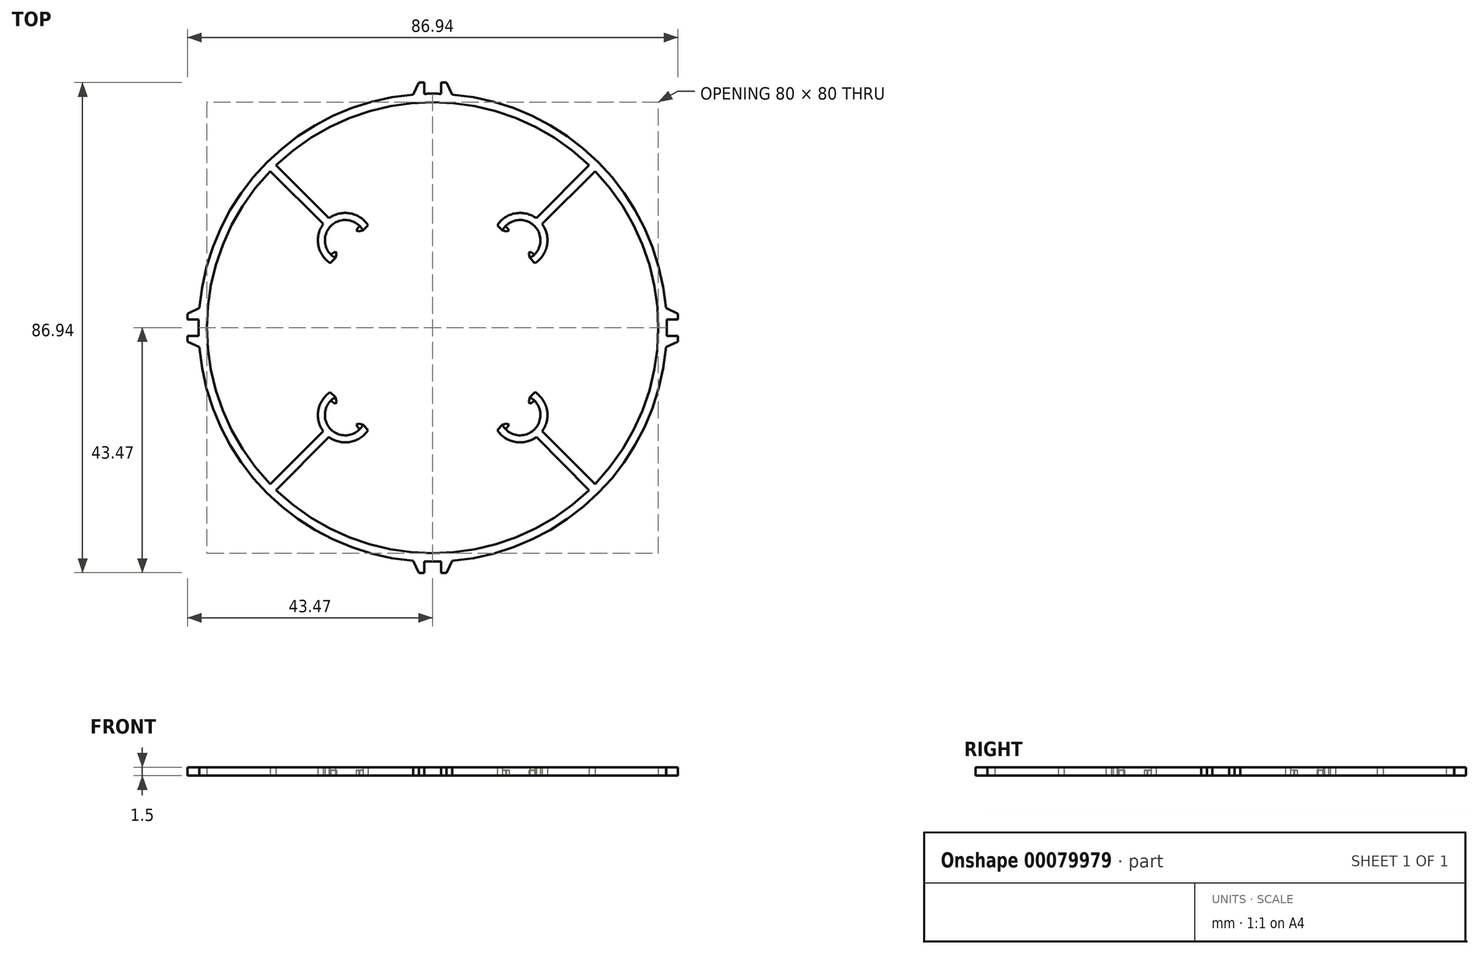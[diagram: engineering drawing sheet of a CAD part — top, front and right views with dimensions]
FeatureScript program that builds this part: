
annotation { "Feature Type Name" : "Feature", "Feature Type Description" : "" }
export const myFeature = defineFeature(function(context is Context, id is Id, definition is map)
    precondition{}
    {
        {
            var Q0;
            Q0=qCreatedBy(makeId("Top.planeOp"),FACE);
            var sketch = newSketch(context, id + "F0", { "sketchPlane" : qUnion([Q0])});
            skLineSegment(sketch, "E0.bottom", {"start": v(-15.5, 15.5) * mm, "end": v(15.5, 15.5) * mm});
            skLineSegment(sketch, "E0.top", {"start": v(-15.5, -15.5) * mm, "end": v(15.5, -15.5) * mm});
            skLineSegment(sketch, "E0.left", {"start": v(-15.5, 15.5) * mm, "end": v(-15.5, -15.5) * mm});
            skLineSegment(sketch, "E0.right", {"start": v(15.5, 15.5) * mm, "end": v(15.5, -15.5) * mm});
            skPoint(sketch, "E0.middle", {"position": v(0, 0) * mm});
            skCircle(sketch, "E1", {"center": v(-15.5, 15.5) * mm, "radius": 15 * mm});
            skCircle(sketch, "E2", {"center": v(15.5, 15.5) * mm, "radius": 15 * mm});
            skCircle(sketch, "E3", {"center": v(-15.5, -15.5) * mm, "radius": 15 * mm});
            skCircle(sketch, "E4", {"center": v(15.5, -15.5) * mm, "radius": 15 * mm});
            skLineSegment(sketch, "E5.bottom", {"start": v(-10, 10) * mm, "end": v(10, 10) * mm});
            skLineSegment(sketch, "E5.top", {"start": v(-10, -10) * mm, "end": v(10, -10) * mm});
            skLineSegment(sketch, "E5.left", {"start": v(-10, 10) * mm, "end": v(-10, -10) * mm});
            skLineSegment(sketch, "E5.right", {"start": v(10, 10) * mm, "end": v(10, -10) * mm});
            skCircle(sketch, "E6", {"center": v(-15.5, 15.5) * mm, "radius": 4.5 * mm});
            skCircle(sketch, "E7", {"center": v(-15.5, 15.5) * mm, "radius": 3.5 * mm});
            skCircle(sketch, "E8", {"center": v(15.5, 15.5) * mm, "radius": 3.5 * mm});
            skCircle(sketch, "E9", {"center": v(15.5, 15.5) * mm, "radius": 4.5 * mm});
            skCircle(sketch, "E10", {"center": v(15.5, -15.5) * mm, "radius": 4.5 * mm});
            skCircle(sketch, "E11", {"center": v(15.5, -15.5) * mm, "radius": 3.5 * mm});
            skCircle(sketch, "E12", {"center": v(-15.5, -15.5) * mm, "radius": 3.5 * mm});
            skCircle(sketch, "E13", {"center": v(-15.5, -15.5) * mm, "radius": 4.5 * mm});
            skLineSegment(sketch, "E14.bottom", {"start": v(-15.5, 15.5) * mm, "end": v(-10.5, 15.5) * mm});
            skLineSegment(sketch, "E14.left", {"start": v(-15.5, 15.5) * mm, "end": v(-15.5, 20.5) * mm});
            skLineSegment(sketch, "E15", {"start": v(-12.32, 18.68) * mm, "end": v(-18.68, 12.32) * mm});
            skLineSegment(sketch, "E16", {"start": v(-17.9, 11.7) * mm, "end": v(-11.7, 17.9) * mm});
            skSolve(sketch);
        }
        {
            var Q0;
            {var subQ1=sQuery(id+"F0.wireOp",EDGE,"E0.bottom");var subQ5=sQuery(id+"F0.wireOp",EDGE,"E14.bottom");var subQ6=makeQuery(id+"F0.imprint","INTERSECT",VERTEX,{"derivedFrom":[subQ1,subQ5]});Q0=makeQuery(id+"F0.imprint","IMPRINT",FACE,{"disambiguationData":[TD([[makeQuery(id+"F0.imprint","IMPRINT",EDGE,{"disambiguationData":[TD([[subQ6,-1.0]])],"derivedFrom":subQ1}),1.0]])]});}
            var sketch = newSketch(context, id + "F1", { "sketchPlane" : qUnion([Q0])});
            skCircle(sketch, "E17", {"center": v(0, 0) * mm, "radius": 41.5 * mm});
            skLineSegment(sketch, "E18", {"start": v(-17.05, 13.08) * mm, "end": v(-17.24, 13.54) * mm});
            skLineSegment(sketch, "E19", {"start": v(-17.24, 13.54) * mm, "end": v(-18.05, 12.95) * mm});
            skLineSegment(sketch, "E20", {"start": v(-18.39, 19.4) * mm, "end": v(-27.75, 28.8) * mm});
            skLineSegment(sketch, "E21", {"start": v(-19.4, 18.39) * mm, "end": v(-28.8, 27.75) * mm});
            skLineSegment(sketch, "E22", {"start": v(-17.25, 12.35) * mm, "end": v(-17.05, 13.08) * mm});
            skArc(sketch, "E23", {"start": v(-11.44, 18.16) * mm, "mid": v(-14.65, 20.27) * mm, "end": v(-18.39, 19.4) * mm});
            skArc(sketch, "E24", {"start": v(-12.95, 18.05) * mm, "mid": v(-18.05, 18.05) * mm, "end": v(-18.05, 12.95) * mm});
            skLineSegment(sketch, "E25.0", {"start": v(-17.9, 11.7) * mm, "end": v(-11.7, 17.9) * mm, "construction": true});
            skLineSegment(sketch, "E26", {"start": v(-12.95, 18.05) * mm, "end": v(-13.54, 17.24) * mm});
            skLineSegment(sketch, "E27", {"start": v(-13.54, 17.24) * mm, "end": v(-13.08, 17.05) * mm});
            skLineSegment(sketch, "E28", {"start": v(-13.08, 17.05) * mm, "end": v(-12.35, 17.25) * mm});
            skLineSegment(sketch, "E29", {"start": v(-12.35, 17.25) * mm, "end": v(-11.7, 17.9) * mm, "construction": true});
            skArc(sketch, "E30", {"start": v(-28.8, 27.75) * mm, "mid": v(-40, 0) * mm, "end": v(-28.8, -27.75) * mm});
            skLineSegment(sketch, "E31", {"start": v(-12.35, 17.25) * mm, "end": v(-11.44, 18.16) * mm});
            skLineSegment(sketch, "E32", {"start": v(-18.16, 11.44) * mm, "end": v(-17.25, 12.35) * mm});
            skArc(sketch, "E33.trimOffspring", {"start": v(-19.4, 18.39) * mm, "mid": v(-20.27, 14.65) * mm, "end": v(-18.16, 11.44) * mm});
            skArc(sketch, "E34.1.0", {"start": v(-18.39, -19.4) * mm, "mid": v(-14.65, -20.27) * mm, "end": v(-11.44, -18.16) * mm});
            skLineSegment(sketch, "E34.1.1", {"start": v(-19.4, -18.39) * mm, "end": v(-28.8, -27.75) * mm});
            skArc(sketch, "E34.1.2", {"start": v(-18.05, -12.95) * mm, "mid": v(-18.05, -18.05) * mm, "end": v(-12.95, -18.05) * mm});
            skLineSegment(sketch, "E34.1.3", {"start": v(-11.7, -17.9) * mm, "end": v(-17.9, -11.7) * mm, "construction": true});
            skArc(sketch, "E34.1.4", {"start": v(-18.16, -11.44) * mm, "mid": v(-20.27, -14.65) * mm, "end": v(-19.4, -18.39) * mm});
            skLineSegment(sketch, "E34.1.5", {"start": v(-18.39, -19.4) * mm, "end": v(-27.75, -28.8) * mm});
            skLineSegment(sketch, "E34.1.6", {"start": v(-18.05, -12.95) * mm, "end": v(-17.24, -13.54) * mm});
            skLineSegment(sketch, "E34.1.7", {"start": v(-13.54, -17.24) * mm, "end": v(-12.95, -18.05) * mm});
            skLineSegment(sketch, "E34.1.8", {"start": v(-17.05, -13.08) * mm, "end": v(-17.25, -12.35) * mm});
            skLineSegment(sketch, "E34.1.9", {"start": v(-17.24, -13.54) * mm, "end": v(-17.05, -13.08) * mm});
            skLineSegment(sketch, "E34.1.10", {"start": v(-11.44, -18.16) * mm, "end": v(-12.35, -17.25) * mm});
            skLineSegment(sketch, "E34.1.11", {"start": v(-12.35, -17.25) * mm, "end": v(-13.08, -17.05) * mm});
            skLineSegment(sketch, "E34.1.12", {"start": v(-17.25, -12.35) * mm, "end": v(-18.16, -11.44) * mm});
            skLineSegment(sketch, "E34.1.13", {"start": v(-13.08, -17.05) * mm, "end": v(-13.54, -17.24) * mm});
            skLineSegment(sketch, "E34.1.14", {"start": v(-17.25, -12.35) * mm, "end": v(-17.9, -11.7) * mm, "construction": true});
            skArc(sketch, "E34.2.0", {"start": v(19.4, -18.39) * mm, "mid": v(20.27, -14.65) * mm, "end": v(18.16, -11.44) * mm});
            skLineSegment(sketch, "E34.2.1", {"start": v(18.39, -19.4) * mm, "end": v(27.75, -28.8) * mm});
            skArc(sketch, "E34.2.2", {"start": v(12.95, -18.05) * mm, "mid": v(18.05, -18.05) * mm, "end": v(18.05, -12.95) * mm});
            skLineSegment(sketch, "E34.2.3", {"start": v(17.9, -11.7) * mm, "end": v(11.7, -17.9) * mm, "construction": true});
            skArc(sketch, "E34.2.4", {"start": v(11.44, -18.16) * mm, "mid": v(14.65, -20.27) * mm, "end": v(18.39, -19.4) * mm});
            skLineSegment(sketch, "E34.2.5", {"start": v(19.4, -18.39) * mm, "end": v(28.8, -27.75) * mm});
            skLineSegment(sketch, "E34.2.6", {"start": v(12.95, -18.05) * mm, "end": v(13.54, -17.24) * mm});
            skLineSegment(sketch, "E34.2.7", {"start": v(17.24, -13.54) * mm, "end": v(18.05, -12.95) * mm});
            skLineSegment(sketch, "E34.2.8", {"start": v(13.08, -17.05) * mm, "end": v(12.35, -17.25) * mm});
            skLineSegment(sketch, "E34.2.9", {"start": v(13.54, -17.24) * mm, "end": v(13.08, -17.05) * mm});
            skLineSegment(sketch, "E34.2.10", {"start": v(18.16, -11.44) * mm, "end": v(17.25, -12.35) * mm});
            skLineSegment(sketch, "E34.2.11", {"start": v(17.25, -12.35) * mm, "end": v(17.05, -13.08) * mm});
            skLineSegment(sketch, "E34.2.12", {"start": v(12.35, -17.25) * mm, "end": v(11.44, -18.16) * mm});
            skLineSegment(sketch, "E34.2.13", {"start": v(17.05, -13.08) * mm, "end": v(17.24, -13.54) * mm});
            skLineSegment(sketch, "E34.2.14", {"start": v(12.35, -17.25) * mm, "end": v(11.7, -17.9) * mm, "construction": true});
            skArc(sketch, "E34.3.0", {"start": v(18.39, 19.4) * mm, "mid": v(14.65, 20.27) * mm, "end": v(11.44, 18.16) * mm});
            skLineSegment(sketch, "E34.3.1", {"start": v(19.4, 18.39) * mm, "end": v(28.8, 27.75) * mm});
            skArc(sketch, "E34.3.2", {"start": v(18.05, 12.95) * mm, "mid": v(18.05, 18.05) * mm, "end": v(12.95, 18.05) * mm});
            skLineSegment(sketch, "E34.3.3", {"start": v(11.7, 17.9) * mm, "end": v(17.9, 11.7) * mm, "construction": true});
            skArc(sketch, "E34.3.4", {"start": v(18.16, 11.44) * mm, "mid": v(20.27, 14.65) * mm, "end": v(19.4, 18.39) * mm});
            skLineSegment(sketch, "E34.3.5", {"start": v(18.39, 19.4) * mm, "end": v(27.75, 28.8) * mm});
            skLineSegment(sketch, "E34.3.6", {"start": v(18.05, 12.95) * mm, "end": v(17.24, 13.54) * mm});
            skLineSegment(sketch, "E34.3.7", {"start": v(13.54, 17.24) * mm, "end": v(12.95, 18.05) * mm});
            skLineSegment(sketch, "E34.3.8", {"start": v(17.05, 13.08) * mm, "end": v(17.25, 12.35) * mm});
            skLineSegment(sketch, "E34.3.9", {"start": v(17.24, 13.54) * mm, "end": v(17.05, 13.08) * mm});
            skLineSegment(sketch, "E34.3.10", {"start": v(11.44, 18.16) * mm, "end": v(12.35, 17.25) * mm});
            skLineSegment(sketch, "E34.3.11", {"start": v(12.35, 17.25) * mm, "end": v(13.08, 17.05) * mm});
            skLineSegment(sketch, "E34.3.12", {"start": v(17.25, 12.35) * mm, "end": v(18.16, 11.44) * mm});
            skLineSegment(sketch, "E34.3.13", {"start": v(13.08, 17.05) * mm, "end": v(13.54, 17.24) * mm});
            skLineSegment(sketch, "E34.3.14", {"start": v(17.25, 12.35) * mm, "end": v(17.9, 11.7) * mm, "construction": true});
            skArc(sketch, "E35.trimOffspring", {"start": v(27.75, 28.8) * mm, "mid": v(0, 40) * mm, "end": v(-27.75, 28.8) * mm});
            skArc(sketch, "E36.trimOffspring", {"start": v(28.8, -27.75) * mm, "mid": v(40, 0) * mm, "end": v(28.8, 27.75) * mm});
            skArc(sketch, "E37.trimOffspring", {"start": v(-27.75, -28.8) * mm, "mid": v(0, -40) * mm, "end": v(27.75, -28.8) * mm});
            skSolve(sketch);
        }
        {
            var Q0;
            Q0=qCreatedBy(makeId("Top.planeOp"),FACE);
            var sketch = newSketch(context, id + "F2", { "sketchPlane" : qUnion([Q0])});
            skLineSegment(sketch, "E38", {"start": v(-1.47, 43.47) * mm, "end": v(-2.47, 43.47) * mm});
            skLineSegment(sketch, "E39", {"start": v(-2.47, 43.47) * mm, "end": v(-3.46, 41.36) * mm});
            skLineSegment(sketch, "E40.MirrorCS", {"start": v(1.47, 43.47) * mm, "end": v(2.47, 43.47) * mm});
            skLineSegment(sketch, "E41.MirrorCS", {"start": v(2.47, 43.47) * mm, "end": v(3.46, 41.36) * mm});
            skLineSegment(sketch, "E42", {"start": v(-1.47, 43.47) * mm, "end": v(-1.47, 41.47) * mm});
            skLineSegment(sketch, "E43", {"start": v(1.47, 43.47) * mm, "end": v(1.47, 41.47) * mm});
            skLineSegment(sketch, "E44.1.0", {"start": v(-43.47, 1.47) * mm, "end": v(-43.47, 2.47) * mm});
            skLineSegment(sketch, "E44.1.1", {"start": v(-43.47, -1.47) * mm, "end": v(-43.47, -2.47) * mm});
            skLineSegment(sketch, "E44.1.2", {"start": v(-43.47, 2.47) * mm, "end": v(-41.36, 3.46) * mm});
            skLineSegment(sketch, "E44.1.3", {"start": v(-43.47, -2.47) * mm, "end": v(-41.36, -3.46) * mm});
            skLineSegment(sketch, "E44.1.4", {"start": v(-43.47, 1.47) * mm, "end": v(-41.47, 1.47) * mm});
            skLineSegment(sketch, "E44.1.5", {"start": v(-43.47, -1.47) * mm, "end": v(-41.47, -1.47) * mm});
            skLineSegment(sketch, "E44.2.0", {"start": v(-1.47, -43.47) * mm, "end": v(-2.47, -43.47) * mm});
            skLineSegment(sketch, "E44.2.1", {"start": v(1.47, -43.47) * mm, "end": v(2.47, -43.47) * mm});
            skLineSegment(sketch, "E44.2.2", {"start": v(-2.47, -43.47) * mm, "end": v(-3.46, -41.36) * mm});
            skLineSegment(sketch, "E44.2.3", {"start": v(2.47, -43.47) * mm, "end": v(3.46, -41.36) * mm});
            skLineSegment(sketch, "E44.2.4", {"start": v(-1.47, -43.47) * mm, "end": v(-1.47, -41.47) * mm});
            skLineSegment(sketch, "E44.2.5", {"start": v(1.47, -43.47) * mm, "end": v(1.47, -41.47) * mm});
            skLineSegment(sketch, "E44.3.0", {"start": v(43.47, -1.47) * mm, "end": v(43.47, -2.47) * mm});
            skLineSegment(sketch, "E44.3.1", {"start": v(43.47, 1.47) * mm, "end": v(43.47, 2.47) * mm});
            skLineSegment(sketch, "E44.3.2", {"start": v(43.47, -2.47) * mm, "end": v(41.36, -3.46) * mm});
            skLineSegment(sketch, "E44.3.3", {"start": v(43.47, 2.47) * mm, "end": v(41.36, 3.46) * mm});
            skLineSegment(sketch, "E44.3.4", {"start": v(43.47, -1.47) * mm, "end": v(41.47, -1.47) * mm});
            skLineSegment(sketch, "E44.3.5", {"start": v(43.47, 1.47) * mm, "end": v(41.47, 1.47) * mm});
            skPoint(sketch, "E44.center", {"position": v(0, 0) * mm});
            skLineSegment(sketch, "E45", {"start": v(-41.47, 1.47) * mm, "end": v(-41.36, 3.46) * mm});
            skLineSegment(sketch, "E46", {"start": v(-41.36, -3.46) * mm, "end": v(-41.47, -1.47) * mm});
            skLineSegment(sketch, "E47", {"start": v(-3.46, 41.36) * mm, "end": v(-1.47, 41.47) * mm});
            skLineSegment(sketch, "E48", {"start": v(1.47, 41.47) * mm, "end": v(3.46, 41.36) * mm});
            skLineSegment(sketch, "E49", {"start": v(41.36, 3.46) * mm, "end": v(41.47, 1.47) * mm});
            skLineSegment(sketch, "E50", {"start": v(41.47, -1.47) * mm, "end": v(41.36, -3.46) * mm});
            skLineSegment(sketch, "E51", {"start": v(1.47, -41.47) * mm, "end": v(3.46, -41.36) * mm});
            skLineSegment(sketch, "E52", {"start": v(-1.47, -41.47) * mm, "end": v(-3.46, -41.36) * mm});
            skSolve(sketch);
        }
        {
            var Q0;
            Q0=qSketchRegion(id+"F1",true);
            extrude(context, id + "F3", {"entities" : qUnion([Q0]), "depth" : 1.5 * mm});
        }
        {
            var Q0;
            Q0=qSketchRegion(id+"F2",true);
            extrude(context, id + "F4", {"entities" : qUnion([Q0]), "operationType" : NewBodyOperationType.ADD, "depth" : 1.5 * mm});
        }
        {
            var Q0;
            Q0=makeQuery(id+"F4.boolean.opBoolean","MERGE",FACE,{"derivedFrom":[makeQuery(id+"F3.opExtrude","CAP_FACE",FACE,{"disambiguationData":[OSD([sQuery(id+"F1.wireOp",EDGE,"E17"),sQuery(id+"F1.wireOp",EDGE,"E18"),sQuery(id+"F1.wireOp",EDGE,"E19"),sQuery(id+"F1.wireOp",EDGE,"E20"),sQuery(id+"F1.wireOp",EDGE,"E21"),sQuery(id+"F1.wireOp",EDGE,"E22"),sQuery(id+"F1.wireOp",EDGE,"E23"),sQuery(id+"F1.wireOp",EDGE,"E24"),sQuery(id+"F1.wireOp",EDGE,"E26"),sQuery(id+"F1.wireOp",EDGE,"E27"),sQuery(id+"F1.wireOp",EDGE,"E28"),sQuery(id+"F1.wireOp",EDGE,"E30"),sQuery(id+"F1.wireOp",EDGE,"E31"),sQuery(id+"F1.wireOp",EDGE,"E32"),sQuery(id+"F1.wireOp",EDGE,"E33.trimOffspring"),sQuery(id+"F1.wireOp",EDGE,"E34.1.0"),sQuery(id+"F1.wireOp",EDGE,"E34.1.1"),sQuery(id+"F1.wireOp",EDGE,"E34.1.2"),sQuery(id+"F1.wireOp",EDGE,"E34.1.4"),sQuery(id+"F1.wireOp",EDGE,"E34.1.5"),sQuery(id+"F1.wireOp",EDGE,"E34.1.6"),sQuery(id+"F1.wireOp",EDGE,"E34.1.7"),sQuery(id+"F1.wireOp",EDGE,"E34.1.8"),sQuery(id+"F1.wireOp",EDGE,"E34.1.9"),sQuery(id+"F1.wireOp",EDGE,"E34.1.10"),sQuery(id+"F1.wireOp",EDGE,"E34.1.11"),sQuery(id+"F1.wireOp",EDGE,"E34.1.12"),sQuery(id+"F1.wireOp",EDGE,"E34.1.13"),sQuery(id+"F1.wireOp",EDGE,"E34.2.0"),sQuery(id+"F1.wireOp",EDGE,"E34.2.1"),sQuery(id+"F1.wireOp",EDGE,"E34.2.2"),sQuery(id+"F1.wireOp",EDGE,"E34.2.4"),sQuery(id+"F1.wireOp",EDGE,"E34.2.5"),sQuery(id+"F1.wireOp",EDGE,"E34.2.6"),sQuery(id+"F1.wireOp",EDGE,"E34.2.7"),sQuery(id+"F1.wireOp",EDGE,"E34.2.8"),sQuery(id+"F1.wireOp",EDGE,"E34.2.9"),sQuery(id+"F1.wireOp",EDGE,"E34.2.10"),sQuery(id+"F1.wireOp",EDGE,"E34.2.11"),sQuery(id+"F1.wireOp",EDGE,"E34.2.12"),sQuery(id+"F1.wireOp",EDGE,"E34.2.13"),sQuery(id+"F1.wireOp",EDGE,"E34.3.0"),sQuery(id+"F1.wireOp",EDGE,"E34.3.1"),sQuery(id+"F1.wireOp",EDGE,"E34.3.2"),sQuery(id+"F1.wireOp",EDGE,"E34.3.4"),sQuery(id+"F1.wireOp",EDGE,"E34.3.5"),sQuery(id+"F1.wireOp",EDGE,"E34.3.6"),sQuery(id+"F1.wireOp",EDGE,"E34.3.7"),sQuery(id+"F1.wireOp",EDGE,"E34.3.8"),sQuery(id+"F1.wireOp",EDGE,"E34.3.9"),sQuery(id+"F1.wireOp",EDGE,"E34.3.10"),sQuery(id+"F1.wireOp",EDGE,"E34.3.11"),sQuery(id+"F1.wireOp",EDGE,"E34.3.12"),sQuery(id+"F1.wireOp",EDGE,"E34.3.13"),sQuery(id+"F1.wireOp",EDGE,"E35.trimOffspring"),sQuery(id+"F1.wireOp",EDGE,"E36.trimOffspring"),sQuery(id+"F1.wireOp",EDGE,"E37.trimOffspring")])],"isStart":false}),makeQuery(id+"F4.opExtrude","CAP_FACE",FACE,{"disambiguationData":[OSD([sQuery(id+"F2.wireOp",EDGE,"E38"),sQuery(id+"F2.wireOp",EDGE,"E39"),sQuery(id+"F2.wireOp",EDGE,"E42"),sQuery(id+"F2.wireOp",EDGE,"E47")])],"isStart":false}),makeQuery(id+"F4.opExtrude","CAP_FACE",FACE,{"disambiguationData":[OSD([sQuery(id+"F2.wireOp",EDGE,"E40.MirrorCS"),sQuery(id+"F2.wireOp",EDGE,"E41.MirrorCS"),sQuery(id+"F2.wireOp",EDGE,"E43"),sQuery(id+"F2.wireOp",EDGE,"E48")])],"isStart":false}),makeQuery(id+"F4.opExtrude","CAP_FACE",FACE,{"disambiguationData":[OSD([sQuery(id+"F2.wireOp",EDGE,"E44.1.0"),sQuery(id+"F2.wireOp",EDGE,"E44.1.2"),sQuery(id+"F2.wireOp",EDGE,"E44.1.4"),sQuery(id+"F2.wireOp",EDGE,"E45")])],"isStart":false}),makeQuery(id+"F4.opExtrude","CAP_FACE",FACE,{"disambiguationData":[OSD([sQuery(id+"F2.wireOp",EDGE,"E44.1.1"),sQuery(id+"F2.wireOp",EDGE,"E44.1.3"),sQuery(id+"F2.wireOp",EDGE,"E44.1.5"),sQuery(id+"F2.wireOp",EDGE,"E46")])],"isStart":false}),makeQuery(id+"F4.opExtrude","CAP_FACE",FACE,{"disambiguationData":[OSD([sQuery(id+"F2.wireOp",EDGE,"E44.2.0"),sQuery(id+"F2.wireOp",EDGE,"E44.2.2"),sQuery(id+"F2.wireOp",EDGE,"E44.2.4"),sQuery(id+"F2.wireOp",EDGE,"E52")])],"isStart":false}),makeQuery(id+"F4.opExtrude","CAP_FACE",FACE,{"disambiguationData":[OSD([sQuery(id+"F2.wireOp",EDGE,"E44.2.1"),sQuery(id+"F2.wireOp",EDGE,"E44.2.3"),sQuery(id+"F2.wireOp",EDGE,"E44.2.5"),sQuery(id+"F2.wireOp",EDGE,"E51")])],"isStart":false}),makeQuery(id+"F4.opExtrude","CAP_FACE",FACE,{"disambiguationData":[OSD([sQuery(id+"F2.wireOp",EDGE,"E44.3.0"),sQuery(id+"F2.wireOp",EDGE,"E44.3.2"),sQuery(id+"F2.wireOp",EDGE,"E44.3.4"),sQuery(id+"F2.wireOp",EDGE,"E50")])],"isStart":false}),makeQuery(id+"F4.opExtrude","CAP_FACE",FACE,{"disambiguationData":[OSD([sQuery(id+"F2.wireOp",EDGE,"E44.3.1"),sQuery(id+"F2.wireOp",EDGE,"E44.3.3"),sQuery(id+"F2.wireOp",EDGE,"E44.3.5"),sQuery(id+"F2.wireOp",EDGE,"E49")])],"isStart":false})]});
            var sketch = newSketch(context, id + "F5", { "sketchPlane" : qUnion([Q0])});
            skPoint(sketch, "E53.0", {"position": v(-15.5, 15.5) * mm});
            skCircle(sketch, "E54", {"center": v(-15.5, 15.5) * mm, "radius": 3.6 * mm});
            skCircle(sketch, "E55.1.0", {"center": v(-15.5, -15.5) * mm, "radius": 3.6 * mm});
            skCircle(sketch, "E55.2.0", {"center": v(15.5, -15.5) * mm, "radius": 3.6 * mm});
            skCircle(sketch, "E55.3.0", {"center": v(15.5, 15.5) * mm, "radius": 3.6 * mm});
            skPoint(sketch, "E55.center", {"position": v(0, 0) * mm});
            skSolve(sketch);
        }
        {
            var Q0;
            Q0=qSketchRegion(id+"F5",true);
            extrude(context, id + "F6", {"entities" : qUnion([Q0]), "operationType" : NewBodyOperationType.REMOVE, "oppositeDirection" : true, "depth" : 0.5 * mm});
        }
    });
